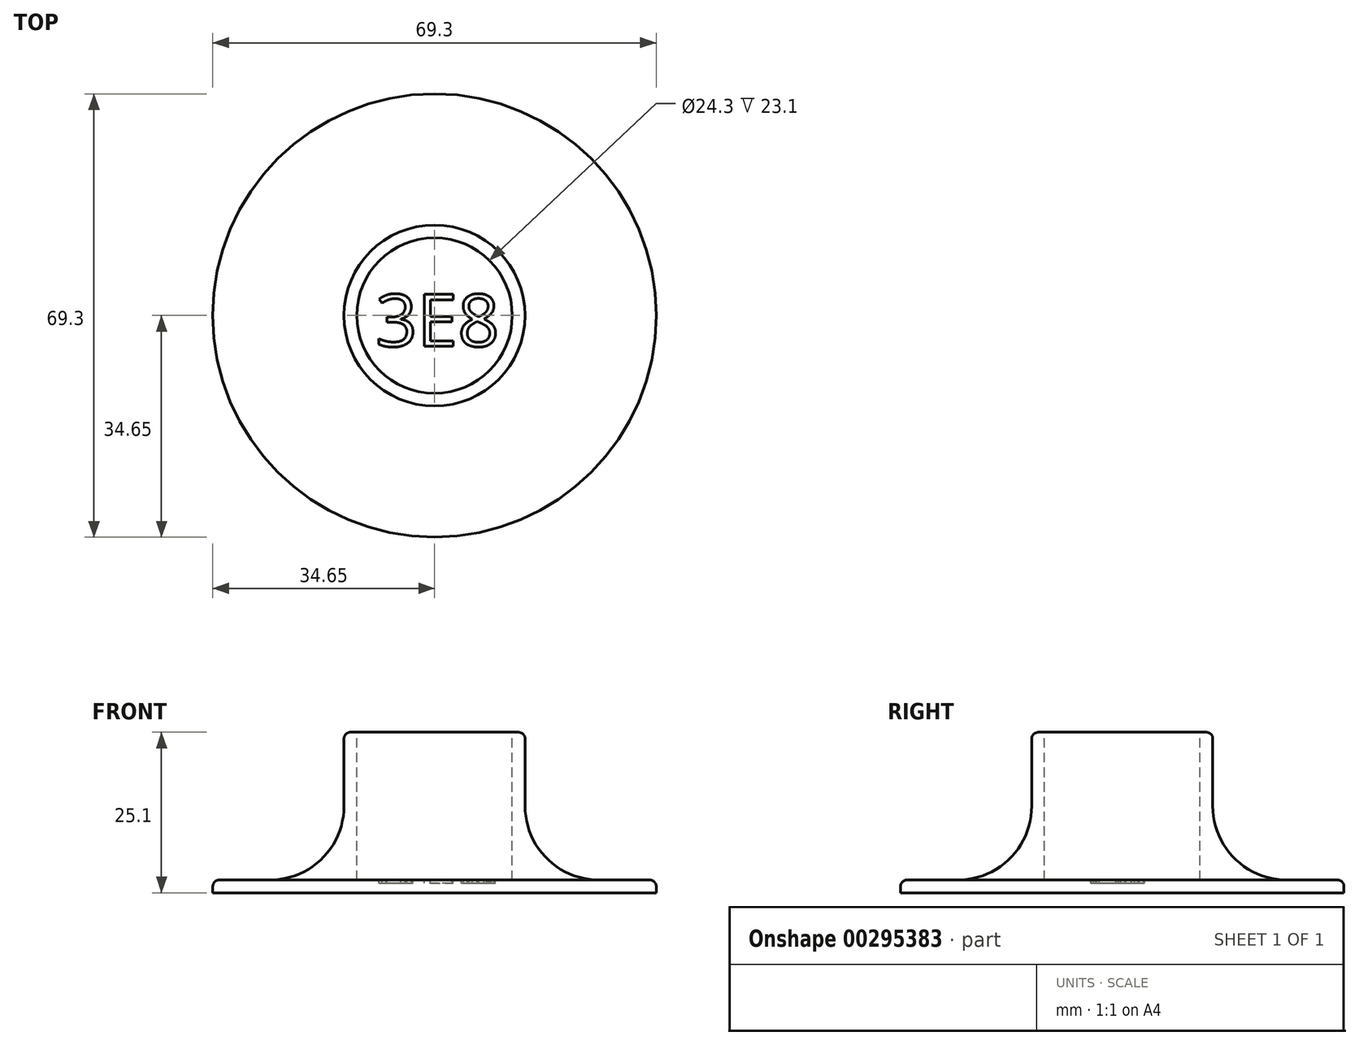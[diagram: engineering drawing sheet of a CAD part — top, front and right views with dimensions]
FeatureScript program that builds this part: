
annotation { "Feature Type Name" : "Feature", "Feature Type Description" : "" }
export const myFeature = defineFeature(function(context is Context, id is Id, definition is map)
    precondition{}
    {
        {
            var Q0;
            Q0=qCreatedBy(makeId("Front.planeOp"),FACE);
            var sketch = newSketch(context, id + "F0", { "sketchPlane" : qUnion([Q0])});
            skLineSegment(sketch, "E0", {"start": v(0, 0) * mm, "end": v(34.65, 0) * mm});
            skLineSegment(sketch, "E1", {"start": v(34.65, 0) * mm, "end": v(34.65, 2) * mm});
            skLineSegment(sketch, "E2", {"start": v(34.65, 2) * mm, "end": v(25.7, 2) * mm});
            skLineSegment(sketch, "E3", {"start": v(14.15, 13.55) * mm, "end": v(14.15, 25.1) * mm});
            skLineSegment(sketch, "E4", {"start": v(14.15, 25.1) * mm, "end": v(12.15, 25.1) * mm});
            skLineSegment(sketch, "E5", {"start": v(12.15, 25.1) * mm, "end": v(12.15, 2) * mm});
            skLineSegment(sketch, "E6", {"start": v(12.15, 2) * mm, "end": v(0, 2) * mm});
            skLineSegment(sketch, "E7", {"start": v(0, 2) * mm, "end": v(0, 0) * mm});
            skArc(sketch, "E8", {"start": v(14.15, 13.55) * mm, "mid": v(17.53, 5.38) * mm, "end": v(25.7, 2) * mm});
            skSolve(sketch);
        }
        {
            var Q0;
            Q0 = qSketchRegion(id + "F0", true);
            var Q1;
            Q1=sQuery(id+"F0.wireOp",EDGE,"E7");
            revolve(context, id + "F1", {"entities" : qUnion([Q0]), "axis" : qUnion([Q1]), "revolveType" : RevolveType.FULL});
        }
        {
            var Q0;
            Q0=makeQuery(id+"F1.opRevolve","SWEPT_FACE",FACE,{"disambiguationData":[OSD([sQuery(id+"F0.wireOp",EDGE,"E6")])]});
            var sketch = newSketch(context, id + "F2", { "sketchPlane" : qUnion([Q0])});
            skText(sketch, "E9", { "text": "3E8", "fontName": "OpenSans-Regular.ttf"});
            const initialGuessF2  = {"E9": [-0.00922, -0.00483, 1, 0, 0.0082]};
            skSetInitialGuess(sketch, initialGuessF2);
            skSolve(sketch);
        }
        {
            var Q0;
            Q0 = qSketchRegion(id + "F2", true);
            extrude(context, id + "F3", {"entities" : qUnion([Q0]), "operationType" : NewBodyOperationType.REMOVE, "oppositeDirection" : true, "depth" : .5 * mm});
        }
        {
            var Q0;
            Q0=makeQuery(id+"F1.opRevolve","SWEPT_EDGE",EDGE,{"disambiguationData":[OSD([sQuery(id+"F0.wireOp",EDGE,"E3"),sQuery(id+"F0.wireOp",EDGE,"E4")])]});
            var Q1;
            Q1=makeQuery(id+"F1.opRevolve","SWEPT_EDGE",EDGE,{"disambiguationData":[OSD([sQuery(id+"F0.wireOp",EDGE,"E1"),sQuery(id+"F0.wireOp",EDGE,"E2")])]});
            fillet(context, id + "F4", {"entities" : qUnion([Q0, Q1]), "radius" : 1 * mm, "tangentPropagation" : true, "allowEdgeOverflow" : false});
        }
    });
